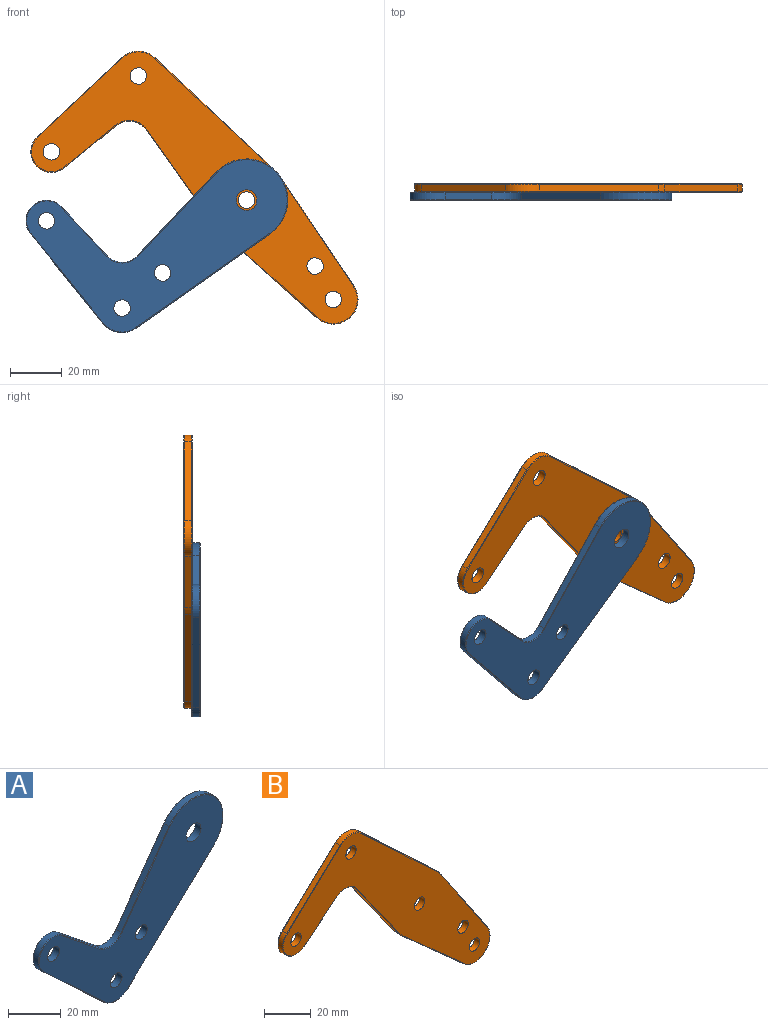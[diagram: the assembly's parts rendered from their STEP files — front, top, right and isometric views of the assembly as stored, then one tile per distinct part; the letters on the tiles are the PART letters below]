
ASSEMBLY  parts=2 mates=1
PART A: 30 faces, bbox 100.9x3.2x75.5 mm
  f0: plane 45.93x43.38mm, normal (0.69,0,-0.73), area 168.5mm2, adj f1,f10,f18,f26
  f1: cylinder r=15.88mm len=28.85mm, axis (0,-1,0), area 141.5mm2, adj f0,f2,f16,f24
  f2: plane 36.43x25.66mm, normal (-0.82,0,0.58), area 118.8mm2, adj f1,f3,f14,f22
  f3: cylinder r=7.94mm len=11.47mm, axis (0,-1,0), area 34.6mm2, adj f2,f4,f15,f23
  f4: plane 20.09x16.18mm, normal (0.63,0,0.78), area 68.8mm2, adj f3,f5,f17,f25
  f5: cylinder r=7.94mm len=13.75mm, axis (0,-1,0), area 65mm2, adj f4,f6,f19,f27
  f6: plane 32.52x30.26mm, normal (-0.68,0,-0.73), area 118.5mm2, adj f5,f10,f21,f29
  f7: cylinder r=3.17mm len=6.35mm, axis (0,-1,0), area 63.3mm2, adj f12,f13
  f8: cylinder r=3.97mm len=7.94mm, axis (0,-1,0), area 79.2mm2, adj f12,f13
  f9: cylinder r=3.17mm len=6.35mm, axis (0,-1,0), area 63.3mm2, adj f12,f13
  f10: cylinder r=9.53mm len=13.03mm, axis (0,-1,0), area 38.3mm2, adj f0,f6,f20,f28
  f11: cylinder r=3.17mm len=6.35mm, axis (0,-1,0), area 63.3mm2, adj f12,f13
  f12: plane 98.48x72.89mm, normal (0,1,0), area 2669.5mm2, adj f7,f8,f9,f11,f22,f23,f24,f25
  f13: plane 98.48x72.89mm, normal (0,-1,0), area 2669.5mm2, adj f7,f8,f9,f11,f14,f15,f16,f17
  f14: cylinder r=0.25mm len=36.57mm, axis (-0.58,0,-0.82), area 17.8mm2, adj f2,f13,f15,f16
  f15: torus R=8.19mm, axis (0,-1,0), area 5.2mm2, adj f3,f13,f14,f17
  f16: torus R=15.62mm, axis (0,-1,0), area 21mm2, adj f1,f13,f14,f18
  f17: cylinder r=0.25mm len=20.25mm, axis (-0.78,0,0.63), area 10.3mm2, adj f4,f13,f15,f19
  f18: cylinder r=0.25mm len=46.11mm, axis (0.73,0,0.69), area 25.2mm2, adj f0,f13,f16,f20
  f19: torus R=7.68mm, axis (0,-1,0), area 9.6mm2, adj f5,f13,f17,f21
  f20: torus R=9.27mm, axis (0,-1,0), area 5.7mm2, adj f10,f13,f18,f21
  f21: cylinder r=0.25mm len=32.69mm, axis (0.73,0,-0.68), area 17.7mm2, adj f6,f13,f19,f20
  f22: cylinder r=0.25mm len=36.57mm, axis (0.58,0,0.82), area 17.8mm2, adj f2,f12,f23,f24
  f23: torus R=8.19mm, axis (0,-1,0), area 5.2mm2, adj f3,f12,f22,f25
  f24: torus R=15.62mm, axis (0,-1,0), area 21mm2, adj f1,f12,f22,f26
  f25: cylinder r=0.25mm len=20.25mm, axis (0.78,0,-0.63), area 10.3mm2, adj f4,f12,f23,f27
  f26: cylinder r=0.25mm len=46.11mm, axis (-0.73,0,-0.69), area 25.2mm2, adj f0,f12,f24,f28
  f27: torus R=7.68mm, axis (0,-1,0), area 9.6mm2, adj f5,f12,f25,f29
  f28: torus R=9.27mm, axis (0,-1,0), area 5.7mm2, adj f10,f12,f26,f29
  f29: cylinder r=0.25mm len=32.69mm, axis (-0.73,0,0.68), area 17.7mm2, adj f6,f12,f27,f28
PART B: 43 faces, bbox 127.5x3.2x106.7 mm
  f0: cylinder r=7.94mm len=13.73mm, axis (0,1,0), area 65mm2, adj f1,f14,f20,f32
  f1: plane 20.03x16.26mm, normal (0.63,0,-0.78), area 68.8mm2, adj f0,f2,f22,f34
  f2: cylinder r=7.94mm len=11.47mm, axis (0,1,0), area 34.6mm2, adj f1,f3,f24,f36
  f3: plane 36.33x25.79mm, normal (-0.82,0,-0.58), area 118.8mm2, adj f2,f4,f26,f38
  f4: cylinder r=15.88mm len=2.67mm, axis (0,1,0), area 9.5mm2, adj f3,f5,f28,f40
  f5: plane 37.62x33.54mm, normal (-0.67,0,-0.75), area 134.4mm2, adj f4,f6,f30,f42
  f6: cylinder r=9.53mm len=15.86mm, axis (0,1,0), area 73.4mm2, adj f5,f7,f29,f41
  f7: plane 41.82x28.13mm, normal (0.83,0,0.56), area 134.4mm2, adj f6,f8,f27,f39
  f8: cylinder r=15.88mm len=2.72mm, axis (0,1,0), area 9.5mm2, adj f7,f9,f25,f37
  f9: plane 46.09x43.21mm, normal (0.68,0,0.73), area 168.5mm2, adj f8,f10,f23,f35
  f10: cylinder r=9.53mm len=13.03mm, axis (0,1,0), area 38.3mm2, adj f9,f14,f21,f33
  f11: cylinder r=3.17mm len=6.35mm, axis (0,1,0), area 63.3mm2, adj f17,f18
  f12: cylinder r=3.17mm len=6.35mm, axis (0,1,0), area 63.3mm2, adj f17,f18
  f13: cylinder r=3.17mm len=6.35mm, axis (0,1,0), area 63.3mm2, adj f17,f18
  f14: plane 32.41x30.38mm, normal (-0.68,0,0.73), area 118.5mm2, adj f0,f10,f19,f31
  f15: cylinder r=3.17mm len=6.35mm, axis (0,1,0), area 63.3mm2, adj f17,f18
  f16: cylinder r=3.17mm len=6.35mm, axis (0,1,0), area 63.3mm2, adj f17,f18
  f17: plane 125.6x104.67mm, normal (0,-1,0), area 3681.8mm2, adj f11,f12,f13,f15,f16,f31,f32,f33
  f18: plane 125.6x104.67mm, normal (0,1,0), area 3681.8mm2, adj f11,f12,f13,f15,f16,f19,f20,f21
  f19: cylinder r=0.25mm len=32.58mm, axis (-0.73,0,-0.68), area 17.7mm2, adj f14,f18,f20,f21
  f20: torus R=7.68mm, axis (0,-1,0), area 9.6mm2, adj f0,f18,f19,f22
  f21: torus R=9.27mm, axis (0,-1,0), area 5.7mm2, adj f10,f18,f19,f23
  f22: cylinder r=0.25mm len=20.19mm, axis (0.78,0,0.63), area 10.3mm2, adj f1,f18,f20,f24
  f23: cylinder r=0.25mm len=46.27mm, axis (-0.73,0,0.68), area 25.2mm2, adj f9,f18,f21,f25
  f24: torus R=8.19mm, axis (0,-1,0), area 5.2mm2, adj f2,f18,f22,f26
  f25: torus R=15.62mm, axis (0,-1,0), area 1.4mm2, adj f8,f18,f23,f27
  f26: cylinder r=0.25mm len=36.48mm, axis (0.58,0,-0.82), area 17.8mm2, adj f3,f18,f24,f28
  f27: cylinder r=0.25mm len=41.96mm, axis (-0.56,0,0.83), area 20.1mm2, adj f7,f18,f25,f29
  f28: torus R=15.62mm, axis (0,-1,0), area 1.4mm2, adj f4,f18,f26,f30
  f29: torus R=9.27mm, axis (0,-1,0), area 10.9mm2, adj f6,f18,f27,f30
  f30: cylinder r=0.25mm len=37.79mm, axis (0.75,0,-0.67), area 20.1mm2, adj f5,f18,f28,f29
  f31: cylinder r=0.25mm len=32.58mm, axis (0.73,0,0.68), area 17.7mm2, adj f14,f17,f32,f33
  f32: torus R=7.68mm, axis (0,-1,0), area 9.6mm2, adj f0,f17,f31,f34
  f33: torus R=9.27mm, axis (0,-1,0), area 5.7mm2, adj f10,f17,f31,f35
  f34: cylinder r=0.25mm len=20.19mm, axis (-0.78,0,-0.63), area 10.3mm2, adj f1,f17,f32,f36
  f35: cylinder r=0.25mm len=46.27mm, axis (0.73,0,-0.68), area 25.2mm2, adj f9,f17,f33,f37
  f36: torus R=8.19mm, axis (0,-1,0), area 5.2mm2, adj f2,f17,f34,f38
  f37: torus R=15.62mm, axis (0,-1,0), area 1.4mm2, adj f8,f17,f35,f39
  f38: cylinder r=0.25mm len=36.48mm, axis (-0.58,0,0.82), area 17.8mm2, adj f3,f17,f36,f40
  f39: cylinder r=0.25mm len=41.96mm, axis (0.56,0,-0.83), area 20.1mm2, adj f7,f17,f37,f41
  f40: torus R=15.62mm, axis (0,-1,0), area 1.4mm2, adj f4,f17,f38,f42
  f41: torus R=9.27mm, axis (0,-1,0), area 10.9mm2, adj f6,f17,f39,f42
  f42: cylinder r=0.25mm len=37.79mm, axis (-0.75,0,0.67), area 20.1mm2, adj f5,f17,f40,f41
PLACE A rot(axis=(0,1,0),8.2deg) t=(0,-6.35,0)mm
PLACE B at identity fixed
MATE revolute B.f4 <-> A.f1  axis (0,1,0) through (0,-3.18,0)mm
